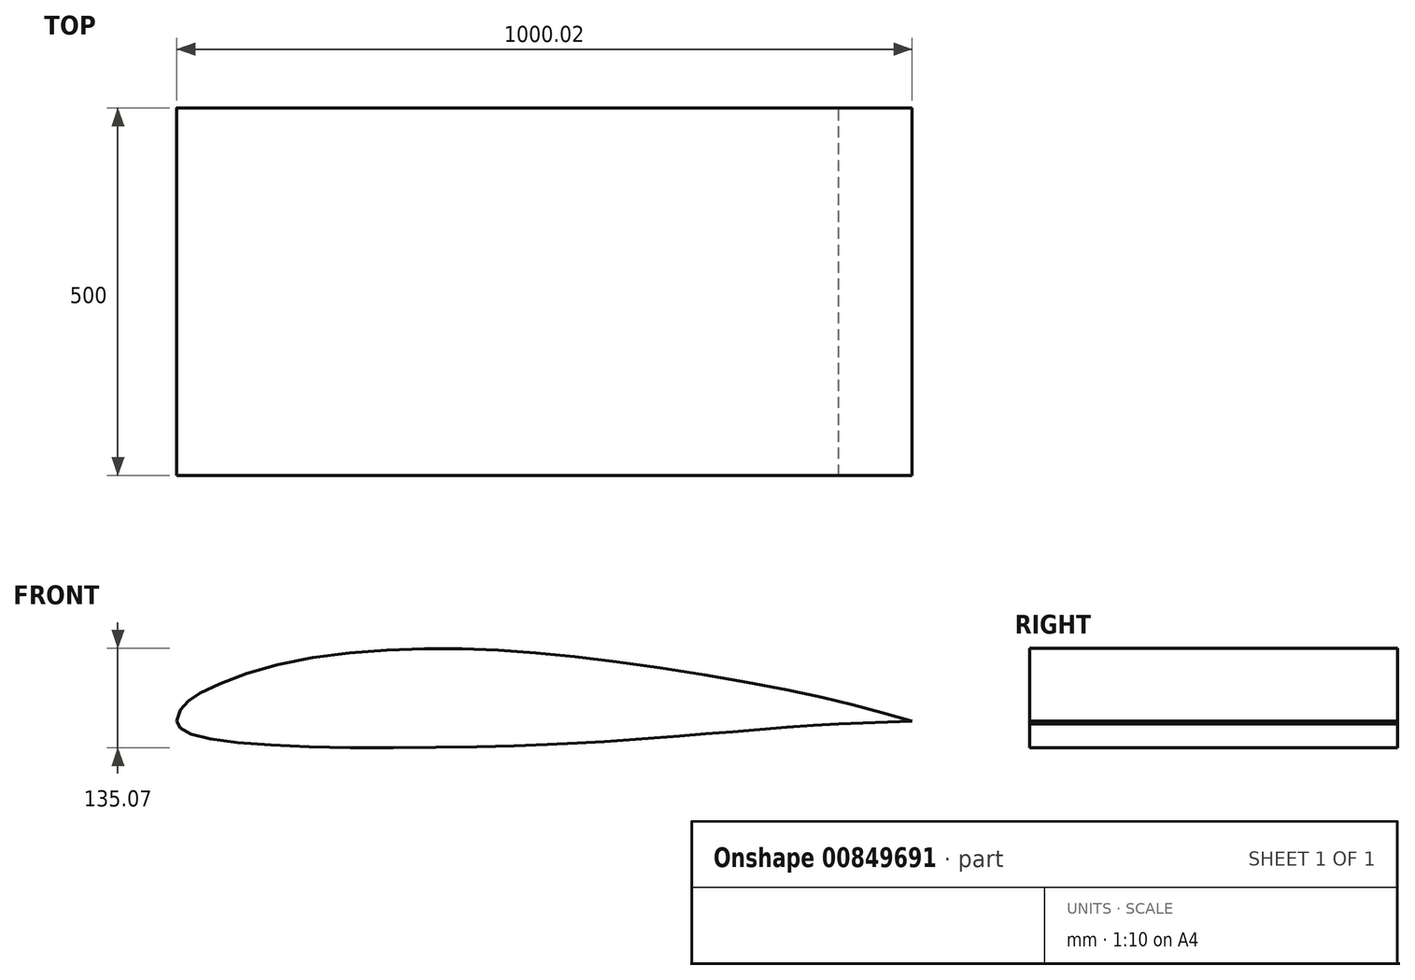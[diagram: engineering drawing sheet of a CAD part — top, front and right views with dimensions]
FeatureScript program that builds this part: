
annotation { "Feature Type Name" : "Feature", "Feature Type Description" : "" }
export const myFeature = defineFeature(function(context is Context, id is Id, definition is map)
    precondition{}
    {
        {
            var Q0;
            Q0=qCreatedBy(makeId("Front.planeOp"),FACE);
            var sketch = newSketch(context, id + "F0", { "sketchPlane" : qUnion([Q0])});
            skLineSegment(sketch, "E0", {"start": v(0, 0) * mm, "end": v(1000, 0) * mm});
            skFitSpline(sketch, "E1", {"points": [v(1000, 0) * mm, v(846.88, 38.7) * mm, v(566.48, 84.34) * mm, v(341.51, 98.47) * mm, v(130.93, 74.83) * mm, v(27.78, 35.7) * mm, v(8.56, 19.99) * mm, v(0, 0) * mm, v(29.91, -21.03) * mm, v(447.3, -34.04) * mm, v(684.53, -20.49) * mm, v(900.4, -4.08) * mm], "startDerivative": vector(-1680.94, 470.21) * mm, "endDerivative": vector(1848.55, 103.27) * mm});
            skLineSegment(sketch, "E2", {"start": v(900.4, -4.08) * mm, "end": v(1000, 0) * mm});
            skSolve(sketch);
        }
        {
            var Q0;
            {var subQ0=sQuery(id+"F0.wireOp",EDGE,"E0");Q0=makeQuery(id+"F0.imprint","IMPRINT",FACE,{"disambiguationData":[TD([[makeQuery(id+"F0.imprint","IMPRINT",EDGE,{"derivedFrom":subQ0}),1.0]])]});}
            var Q1;
            {var subQ0=sQuery(id+"F0.wireOp",EDGE,"E0");Q1=makeQuery(id+"F0.imprint","IMPRINT",FACE,{"disambiguationData":[TD([[makeQuery(id+"F0.imprint","IMPRINT",EDGE,{"derivedFrom":subQ0}),-1.0]])]});}
            extrude(context, id + "F1", {"entities" : qUnion([Q0, Q1]), "depth" : 500 * mm, "offsetDistance" : 25 * mm});
        }
    });
